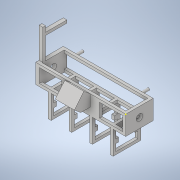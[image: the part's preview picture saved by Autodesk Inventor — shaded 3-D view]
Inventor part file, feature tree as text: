
AUTODESK INVENTOR PART (.ipt)
format: ipt  version: 2021 (Build 250183000, 183)  size: 664,576 bytes
history: native  units: mm
features: sketch x44, extrude x41, plane x1, loft x1
ambient origin geometry x8: Origin, YZ Plane, XZ Plane, XY Plane, X Axis, Y Axis, Z Axis, Center Point
bodies: Solid1 (feature_tree)
feature tree (87):
  extrude  "Extrusion1"  Depth=140.0mm
  extrude  "Extrusion2"  Depth=20.0mm
  extrude  "Extrusion3"  Depth=20.0mm
  extrude  "Extrusion4"  Depth=200.0mm TaperAngle=0.0deg
  extrude  "Extrusion5"  Depth=20.0mm
  extrude  "Extrusion6"  Depth=20.0mm
  extrude  "Extrusion7"  Depth=200.0mm
  extrude  "Extrusion8"  Depth=146.467mm TaperAngle=0.0deg
  extrude  "Extrusion9"  Depth=20.0mm
  extrude  "Extrusion10"  Depth=20.0mm
  extrude  "Extrusion11"  Depth=10.0mm TaperAngle=0.0deg
  extrude  "Extrusion13"  Depth=200.0mm TaperAngle=0.0deg
  extrude  "Extrusion14"  Depth=140.0mm
  extrude  "Extrusion15"  Depth=20.0mm
  extrude  "Extrusion16"  Depth=20.0mm
  extrude  "Extrusion17"  Depth=160.0mm TaperAngle=0.0deg
  extrude  "Extrusion18"  Depth=20.0mm
  extrude  "Extrusion19"  Depth=20.0mm
  extrude  "Extrusion21"  Depth=900.0mm TaperAngle=0.0deg
  extrude  "Extrusion22"  Depth=10.0mm TaperAngle=0.0deg
  sketch  "Sketch25"  dims[d69=10.0mm d70=0.0mm d73=150.0mm d74=0.0mm]
  extrude  "Extrusion26"  Depth=150.0mm TaperAngle=0.0deg
  extrude  "Extrusion27"  Depth=20.0mm
  extrude  "Extrusion28"  Depth=20.0mm
  extrude  "Extrusion29"  Depth=20.0mm
  extrude  "Extrusion30"  Depth=20.0mm
  extrude  "Extrusion31"  Depth=130.0mm TaperAngle=0.0deg
  extrude  "Extrusion32"  Depth=20.0mm
  extrude  "Extrusion33"  Depth=20.0mm
  extrude  "Extrusion34"  Depth=20.0mm
  extrude  "Extrusion35"  Depth=130.0mm TaperAngle=0.0deg
  extrude  "Extrusion36"  Depth=20.0mm
  sketch  "Sketch44"  dims[d126=20.0mm d127=130.0mm]
  plane  "Work Plane2"
  loft  "Loft1"
  extrude  "Extrusion37"  Depth=130.0mm
  extrude  "Extrusion38"  Depth=130.0mm
  extrude  "Extrusion39"  Depth=20.0mm TaperAngle=0.0deg
  extrude  "Extrusion40"  Depth=20.0mm TaperAngle=0.0deg
  extrude  "Extrusion41"  Depth=20.0mm TaperAngle=0.0deg
  extrude  "Extrusion42"  Depth=70.0mm
  extrude  "Extrusion44"  Depth=70.0mm
  extrude  "Extrusion45"  Depth=70.0mm
  extrude  "Extrusion47"  Depth=70.0mm
  extrude  "Extrusion48"  Depth=20.0mm TaperAngle=0.0deg
  sketch  "Sketch1"  dims[d0=140.0mm d1=500.0mm]
  sketch  "Sketch2"  dims[d2=200.0mm d3=0.0mm d4=20.0mm]
  sketch  "Sketch3"  dims[d5=20.0mm d6=20.0mm]
  sketch  "Sketch4"  dims[d7=20.0mm d8=200.0mm d9=0.0mm]
  sketch  "Sketch5"  dims[d10=20.0mm d11=20.0mm]
  sketch  "Sketch7"  dims[d12=20.0mm d13=20.0mm]
  sketch  "Sketch8"  dims[d14=200.0mm d15=0.0mm d16=47.626mm]
  sketch  "Sketch9"  dims[d17=900.0mm d18=0.0mm d19=146.467mm d20=0.0mm]
  sketch  "Sketch10"  dims[d25=146.467mm d26=0.0mm d27=20.0mm]
  sketch  "Sketch11"  dims[d28=600.0mm d29=0.0mm d30=20.0mm]
  sketch  "Sketch12"  dims[d31=600.0mm d32=0.0mm d33=10.0mm d34=0.0mm]
  sketch  "Sketch14"  dims[d35=3.764mm d36=0.0mm d37=200.0mm d38=0.0mm]
  sketch  "Sketch15"  dims[d47=200.0mm d48=140.0mm]
  sketch  "Sketch16"  dims[d49=160.0mm d50=0.0mm d51=20.0mm]
  sketch  "Sketch17"  dims[d52=20.0mm d53=20.0mm]
  sketch  "Sketch18"  dims[d54=20.0mm d55=160.0mm d56=0.0mm]
  sketch  "Sketch19"  dims[d57=20.0mm d58=20.0mm]
  sketch  "Sketch20"  dims[d59=20.0mm d60=20.0mm]
  sketch  "Sketch23"  dims[d61=900.0mm d62=0.0mm d63=900.0mm d64=0.0mm]
  sketch  "Sketch24"  dims[d65=10.0mm d66=0.0mm d67=10.0mm d68=0.0mm]
  sketch  "Sketch32"  dims[d75=150.0mm d76=0.0mm d101=20.0mm]
  sketch  "Sketch33"  dims[d102=91.3515mm d103=20.0mm]
  sketch  "Sketch34"  dims[d104=130.0mm d105=20.0mm]
  sketch  "Sketch35"  dims[d106=130.0mm d107=20.0mm]
  sketch  "Sketch36"  dims[d108=130.0mm d109=110.0mm d110=0.0mm]
  sketch  "Sketch37"  dims[d111=91.3515mm d112=20.0mm]
  sketch  "Sketch39"  dims[d113=130.0mm d114=20.0mm]
  sketch  "Sketch40"  dims[d115=130.0mm d116=20.0mm]
  sketch  "Sketch41"  dims[d117=130.0mm d118=110.0mm d119=0.0mm]
  sketch  "Sketch42"  dims[d121=20.0mm d122=20.0mm]
  sketch  "Sketch43"  dims[d123=20.0mm d124=900.0mm d125=0.0mm]
  sketch  "Sketch45"  dims[d128=20.0mm d129=130.0mm]
  sketch  "Sketch46"  dims[d130=20.0mm d131=20.0mm d132=0.0mm]
  sketch  "Sketch47"  dims[d134=20.0mm d135=20.0mm d136=0.0mm]
  sketch  "Sketch48"  dims[d137=10.0mm d138=20.0mm d139=0.0mm]
  sketch  "Sketch49"  dims[d140=70.0mm d141=70.0mm]
  sketch  "Sketch50"  dims[d142=70.0mm d143=70.0mm]
  sketch  "Sketch51"  dims[d144=70.0mm d145=70.0mm]
  sketch  "Sketch53"  dims[d146=20.0mm d147=0.0mm d148=70.0mm]
  sketch  "Sketch55"  dims[d149=70.0mm d150=20.0mm d151=0.0mm]
  sketch  "Sketch56"  dims[d152=20.0mm d153=0.0mm]
  sketch  "Sketch57"  dims[d155=190.0mm d156=20.0mm d157=0.0mm d158=0.0mm d159=190.0mm d160=20.0mm d161=0.0mm d162=20.0mm d163=20.0mm d164=70.0mm d165=232.703mm d166=210.0mm d167=0.0mm d168=90.0deg d169=0.0mm d170=90.0deg d171=55.0mm d172=60.0mm d173=0.0mm d174=232.707mm d175=30.0mm d176=0.0mm d177=30.0mm d178=30.0mm d179=30.0mm d180=0.0mm d181=18.0mm d182=91.5mm d183=10.0mm d184=18.0mm d185=85.0mm d186=10.0mm d187=50.0mm d188=0.0mm d189=30.0mm d190=0.0mm d191=20.0mm d192=30.0mm d193=0.0mm d199=20.0mm d200=45.0mm d201=179.0mm d202=0.0mm d203=20.0mm d204=155.004mm d205=0.0mm d208=41.015mm d209=0.0mm d210=17.0mm d211=17.0mm d212=41.015mm d213=0.0mm d78=0.5mm d79=0.872665mm d80=0.5mm d81=0.872665mm d96=0.5mm d97=0.872665mm d98=0.5mm d99=0.872665mm d214=0.5mm d215=0.872665mm]
